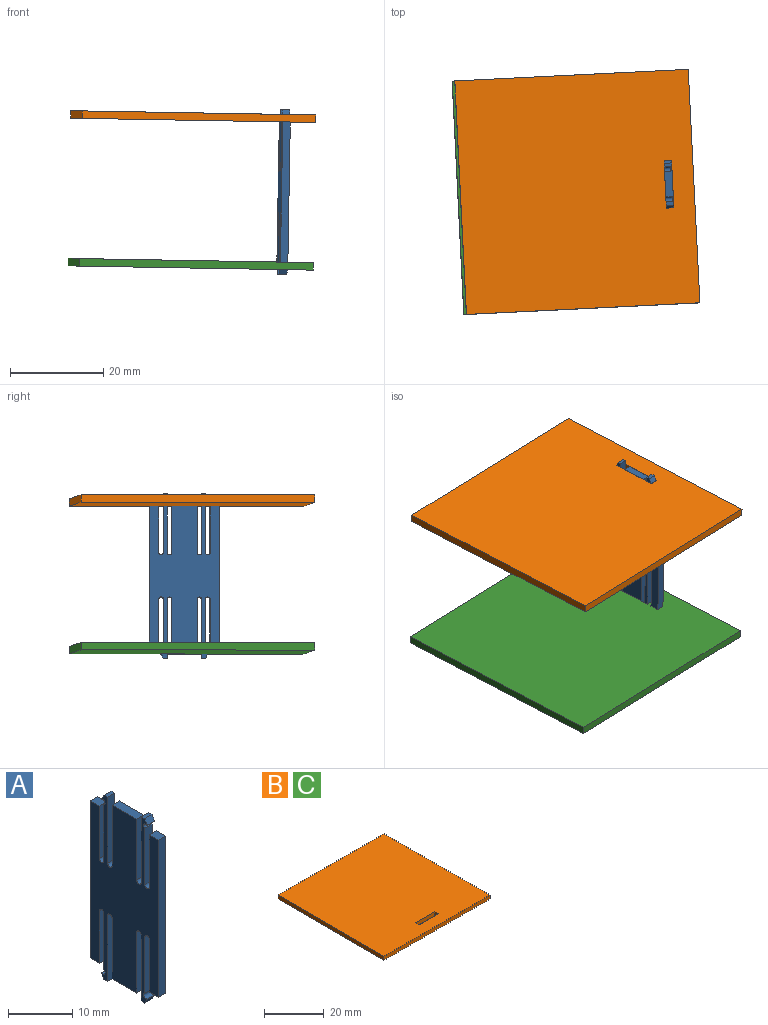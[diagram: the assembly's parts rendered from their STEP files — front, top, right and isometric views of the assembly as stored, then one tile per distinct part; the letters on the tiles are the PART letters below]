
ASSEMBLY  parts=3 mates=6
PART A: 50 faces, bbox 1.6x15x35.2 mm
  f0: plane 35.2x15mm, normal (1,0,0), area 393mm2, adj f2,f3,f4,f5,f6,f7,f8,f9
  f1: plane 35.2x15mm, normal (-1,0,0), area 393mm2, adj f2,f3,f4,f5,f6,f7,f8,f9
  f2: plane 10.75x1.6mm, normal (0,-1,0), area 17.2mm2, adj f0,f1,f39,f48
  f3: plane 10.75x1.6mm, normal (0,1,0), area 17.2mm2, adj f0,f1,f40,f44
  f4: plane 1.6x0.07mm, normal (0,0,-1), area 0.1mm2, adj f0,f1,f30,f40
  f5: plane 1.6x0.07mm, normal (0,0,1), area 0.1mm2, adj f0,f1,f32,f39
  f6: plane 2x1.6mm, normal (0,0,1), area 3.2mm2, adj f0,f1,f11,f21
  f7: plane 2x1.6mm, normal (0,0,-1), area 3.2mm2, adj f0,f1,f11,f19
  f8: plane 2x1.6mm, normal (0,0,1), area 3.2mm2, adj f0,f1,f9,f13
  f9: plane 30x1.6mm, normal (0,-1,0), area 48mm2, adj f0,f1,f8,f10
  f10: plane 2x1.6mm, normal (0,0,-1), area 3.2mm2, adj f0,f1,f9,f14
  f11: plane 30x1.6mm, normal (0,1,0), area 48mm2, adj f0,f1,f6,f7
  f12: plane 10.75x1.6mm, normal (0,-1,0), area 17.2mm2, adj f0,f1,f41,f49
  f13: plane 10x1.6mm, normal (0,1,0), area 16mm2, adj f0,f1,f8,f49
  f14: plane 10x1.6mm, normal (0,1,0), area 16mm2, adj f0,f1,f10,f48
  f15: plane 12.6x1.6mm, normal (0,1,0), area 20.2mm2, adj f0,f1,f33,f47
  f16: plane 11.6x1.6mm, normal (0,-1,0), area 18.6mm2, adj f0,f1,f34,f47
  f17: plane 12.6x1.6mm, normal (0,-1,0), area 20.2mm2, adj f0,f1,f36,f46
  f18: plane 11.6x1.6mm, normal (0,1,0), area 18.6mm2, adj f0,f1,f34,f46
  f19: plane 10x1.6mm, normal (0,-1,0), area 16mm2, adj f0,f1,f7,f45
  f20: plane 10.75x1.6mm, normal (0,1,0), area 17.2mm2, adj f0,f1,f38,f45
  f21: plane 10x1.6mm, normal (0,-1,0), area 16mm2, adj f0,f1,f6,f44
  f22: plane 12.6x1.6mm, normal (0,-1,0), area 20.2mm2, adj f0,f1,f31,f43
  f23: plane 11.6x1.6mm, normal (0,1,0), area 18.6mm2, adj f0,f1,f29,f43
  f24: plane 11.6x1.6mm, normal (0,-1,0), area 18.6mm2, adj f0,f1,f29,f42
  f25: plane 12.6x1.6mm, normal (0,1,0), area 20.2mm2, adj f0,f1,f27,f42
  f26: plane 1.6x0.07mm, normal (0,0,-1), area 0.1mm2, adj f0,f1,f28,f41
  f27: plane 1.6x0.8mm, normal (0,0,1), area 1.3mm2, adj f0,f1,f25,f28
  f28: plane 1.6x1mm, normal (0,-0.86,0.51), area 1.9mm2, adj f0,f1,f26,f27
  f29: plane 5.4x1.6mm, normal (0,0,1), area 8.6mm2, adj f0,f1,f23,f24
  f30: plane 1.6x1mm, normal (0,0.86,0.51), area 1.9mm2, adj f0,f1,f4,f31
  f31: plane 1.6x0.8mm, normal (0,0,1), area 1.3mm2, adj f0,f1,f22,f30
  f32: plane 1.6x1mm, normal (0,-0.86,-0.51), area 1.9mm2, adj f0,f1,f5,f33
  f33: plane 1.6x0.8mm, normal (0,0,-1), area 1.3mm2, adj f0,f1,f15,f32
  f34: plane 5.4x1.6mm, normal (0,0,-1), area 8.6mm2, adj f0,f1,f16,f18
  f35: plane 1.6x0.07mm, normal (0,0,1), area 0.1mm2, adj f0,f1,f37,f38
  f36: plane 1.6x0.8mm, normal (0,0,-1), area 1.3mm2, adj f0,f1,f17,f37
  f37: plane 1.6x1mm, normal (0,0.86,-0.51), area 1.9mm2, adj f0,f1,f35,f36
  f38: cylinder r=0.5mm len=1.6mm, axis (1,0,0), area 2.5mm2, adj f0,f1,f20,f35
  f39: cylinder r=0.5mm len=1.6mm, axis (1,0,0), area 2.5mm2, adj f0,f1,f2,f5
  f40: cylinder r=0.5mm len=1.6mm, axis (1,0,0), area 2.5mm2, adj f0,f1,f3,f4
  f41: cylinder r=0.5mm len=1.6mm, axis (1,0,0), area 2.5mm2, adj f0,f1,f12,f26
  f42: cylinder r=0.5mm len=1.6mm, axis (1,0,0), area 2.5mm2, adj f0,f1,f24,f25
  f43: cylinder r=0.5mm len=1.6mm, axis (1,0,0), area 2.5mm2, adj f0,f1,f22,f23
  f44: cylinder r=0.5mm len=1.6mm, axis (1,0,0), area 2.5mm2, adj f0,f1,f3,f21
  f45: cylinder r=0.5mm len=1.6mm, axis (1,0,0), area 2.5mm2, adj f0,f1,f19,f20
  f46: cylinder r=0.5mm len=1.6mm, axis (1,0,0), area 2.5mm2, adj f0,f1,f17,f18
  f47: cylinder r=0.5mm len=1.6mm, axis (1,0,0), area 2.5mm2, adj f0,f1,f15,f16
  f48: cylinder r=0.5mm len=1.6mm, axis (1,0,0), area 2.5mm2, adj f0,f1,f2,f14
  f49: cylinder r=0.5mm len=1.6mm, axis (1,0,0), area 2.5mm2, adj f0,f1,f12,f13
PART B: 10 faces, bbox 50x50x1.6 mm
  f0: plane 50x1.6mm, normal (0,1,0), area 80mm2, adj f1,f3,f4,f5
  f1: plane 50x1.6mm, normal (-1,0,0), area 80mm2, adj f0,f2,f4,f5
  f2: plane 50x1.6mm, normal (0,-1,0), area 80mm2, adj f1,f3,f4,f5
  f3: plane 50x1.6mm, normal (1,0,0), area 80mm2, adj f0,f2,f4,f5
  f4: plane 50x50mm, normal (0,0,1), area 2485.6mm2, adj f0,f1,f2,f3,f6,f7,f8,f9
  f5: plane 50x50mm, normal (0,0,-1), area 2485.6mm2, adj f0,f1,f2,f3,f6,f7,f8,f9
  f6: plane 1.6x1.6mm, normal (1,0,0), area 2.6mm2, adj f4,f5,f7,f9
  f7: plane 9x1.6mm, normal (0,1,0), area 14.4mm2, adj f4,f5,f6,f8
  f8: plane 1.6x1.6mm, normal (-1,0,0), area 2.6mm2, adj f4,f5,f7,f9
  f9: plane 9x1.6mm, normal (0,-1,0), area 14.4mm2, adj f4,f5,f6,f8
PART C: same geometry as B
PLACE A rot(axis=(0.01,0.33,0.94),3deg) t=(66.85,-7.29,74.13)mm
PLACE B rot(axis=(0.01,0.01,1),92.9deg) t=(74.41,-25.13,104.01)mm
PLACE C rot(axis=(0.01,0.01,1),92.9deg) t=(73.86,-25.13,72.41)mm
MATE planar C.f6 <-> A.f2  axis (-0.05,1,0) through (67.48,-4.25,73.32)mm
MATE planar A.f34 <-> C.f5  axis (-0.02,0,-1) through (67.24,0.25,72.53)mm
MATE planar A.f29 <-> B.f4  axis (0.02,0,1) through (68.62,0.28,105.71)mm
MATE planar C.f9 <-> A.f1  axis (1,0.05,-0.02) through (66.46,0.21,73.34)mm
MATE planar B.f1 <-> C.f1  axis (0.05,-1,0) through (49.46,-26.38,105.24)mm
MATE planar B.f9 <-> A.f1  axis (1,0.05,-0.02) through (67.01,0.2,104.94)mm
